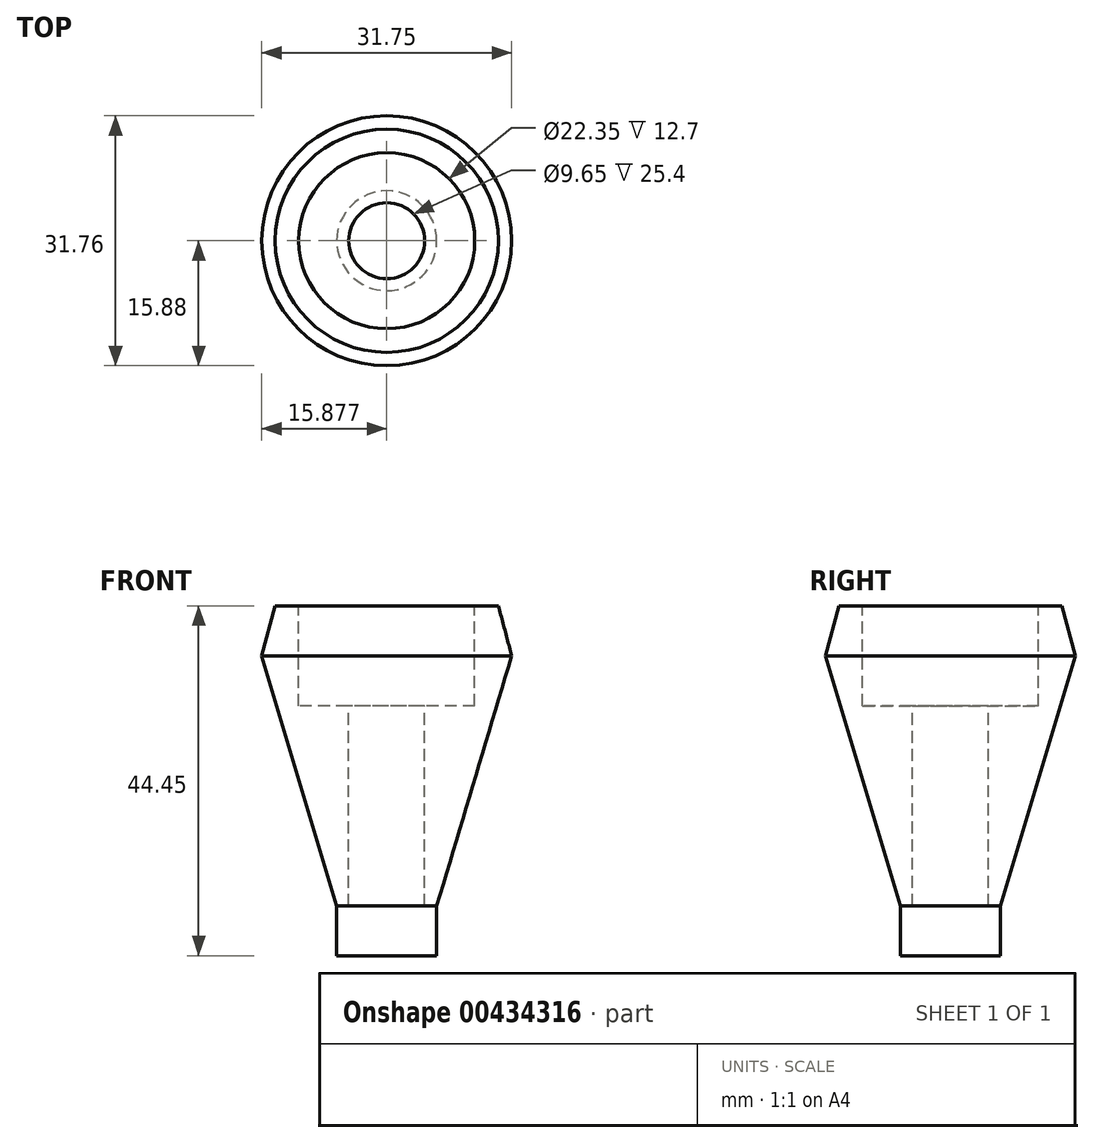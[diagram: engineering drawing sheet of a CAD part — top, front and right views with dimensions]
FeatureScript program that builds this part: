
annotation { "Feature Type Name" : "Feature", "Feature Type Description" : "" }
export const myFeature = defineFeature(function(context is Context, id is Id, definition is map)
    precondition{}
    {
        {
            var Q0;
            Q0=qCreatedBy(makeId("Front.planeOp"),FACE);
            var sketch = newSketch(context, id + "F0", { "sketchPlane" : qUnion([Q0])});
            skLineSegment(sketch, "E0", {"start": v(14.52, 0) * mm, "end": v(20.87, 0) * mm});
            skLineSegment(sketch, "E1", {"start": v(20.87, 0) * mm, "end": v(20.87, 6.35) * mm});
            skLineSegment(sketch, "E2", {"start": v(20.87, 6.35) * mm, "end": v(30.4, 38.1) * mm});
            skLineSegment(sketch, "E3", {"start": v(30.4, 38.1) * mm, "end": v(28.7, 44.45) * mm});
            skLineSegment(sketch, "E4", {"start": v(28.7, 44.45) * mm, "end": v(14.52, 44.45) * mm});
            skLineSegment(sketch, "E5", {"start": v(14.52, 44.45) * mm, "end": v(14.52, 0) * mm});
            skLineSegment(sketch, "E6", {"start": v(30.4, 38.1) * mm, "end": v(30.4, 59.53) * mm, "construction": true});
            skSolve(sketch);
        }
        {
            var Q0;
            Q0=qSketchRegion(id+"F0",true);
            var Q1;
            Q1=sQuery(id+"F0.wireOp",EDGE,"E5");
            revolve(context, id + "F1", {"entities" : qUnion([Q0]), "axis" : qUnion([Q1]), "revolveType" : RevolveType.FULL});
        }
        {
            var Q0;
            Q0=makeQuery(id+"F1.opRevolve","SWEPT_FACE",FACE,{"disambiguationData":[OSD([sQuery(id+"F0.wireOp",EDGE,"E4")])]});
            var sketch = newSketch(context, id + "F2", { "sketchPlane" : qUnion([Q0])});
            skPoint(sketch, "E7", {"position": v(14.52, 0) * mm});
            skCircle(sketch, "E8", {"center": v(14.52, 0) * mm, "radius": 4.83 * mm});
            skCircle(sketch, "E9", {"center": v(14.52, 0) * mm, "radius": 11.18 * mm});
            skSolve(sketch);
        }
        {
            var Q0;
            Q0=makeQuery(id+"F2.imprint","IMPRINT",FACE,{"disambiguationData":[TD([[makeQuery(id+"F2.imprint","IMPRINT",EDGE,{"derivedFrom":sQuery(id+"F2.wireOp",EDGE,"E8")}),1.0]])]});
            extrude(context, id + "F3", {"entities" : qUnion([Q0]), "operationType" : NewBodyOperationType.REMOVE, "oppositeDirection" : true, "depth" : 38.1 * mm});
        }
        {
            var Q0;
            Q0=makeQuery(id+"F2.imprint","IMPRINT",FACE,{"disambiguationData":[TD([[makeQuery(id+"F2.imprint","IMPRINT",EDGE,{"derivedFrom":sQuery(id+"F2.wireOp",EDGE,"E8")}),-1.0]])]});
            extrude(context, id + "F4", {"entities" : qUnion([Q0]), "operationType" : NewBodyOperationType.REMOVE, "oppositeDirection" : true, "depth" : 12.7 * mm});
        }
    });
